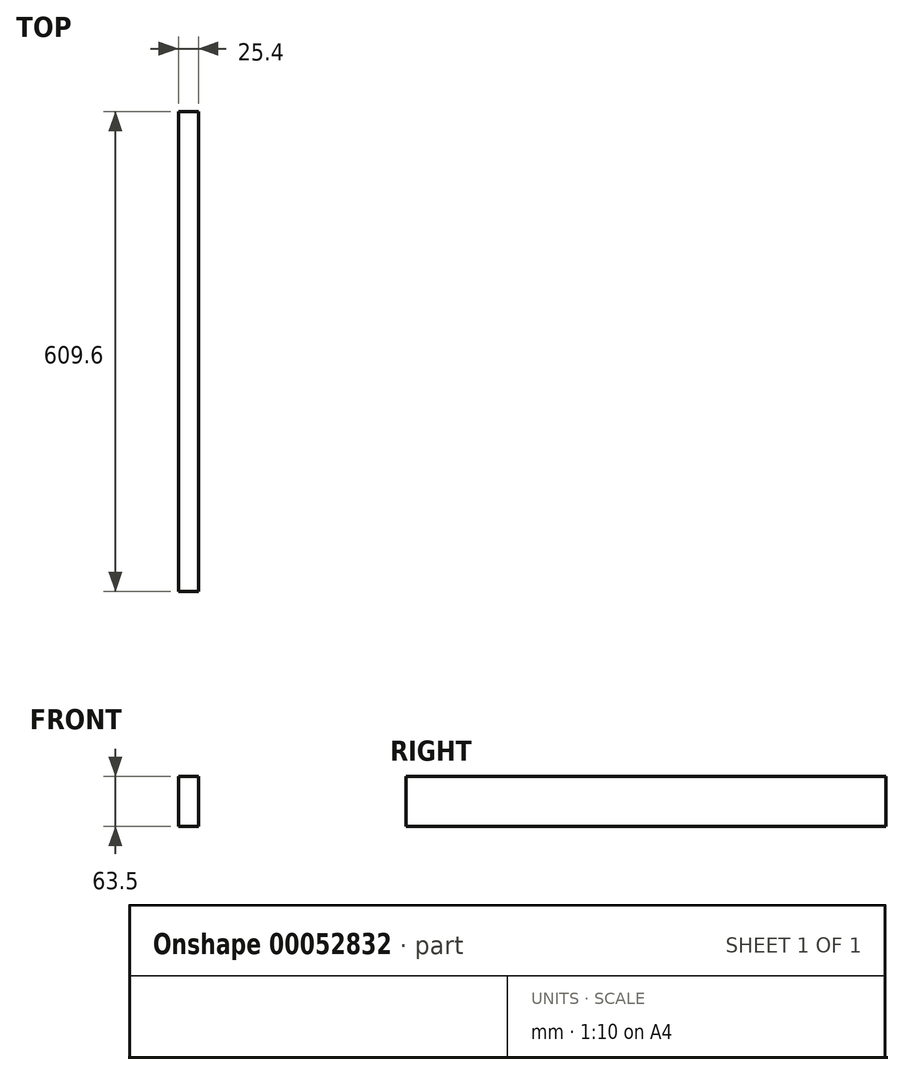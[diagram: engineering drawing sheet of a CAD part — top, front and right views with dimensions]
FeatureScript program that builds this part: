
annotation { "Feature Type Name" : "Feature", "Feature Type Description" : "" }
export const myFeature = defineFeature(function(context is Context, id is Id, definition is map)
    precondition{}
    {
        {
            var Q0;
            Q0=qCreatedBy(makeId("Right.planeOp"),FACE);
            var sketch = newSketch(context, id + "F0", { "sketchPlane" : qUnion([Q0])});
            skLineSegment(sketch, "E0.bottom", {"start": v(559.71, 68.47) * mm, "end": v(1169.31, 68.47) * mm});
            skLineSegment(sketch, "E0.top", {"start": v(559.71, 4.97) * mm, "end": v(1169.31, 4.97) * mm});
            skLineSegment(sketch, "E0.left", {"start": v(559.71, 68.47) * mm, "end": v(559.71, 4.97) * mm});
            skLineSegment(sketch, "E0.right", {"start": v(1169.31, 68.47) * mm, "end": v(1169.31, 4.97) * mm});
            skSolve(sketch);
        }
        {
            var Q0;
            Q0 = qSketchRegion(id + "F0", true);
            extrude(context, id + "F1", {"entities" : qUnion([Q0]), "depth" : 25.4 * mm});
        }
    });
